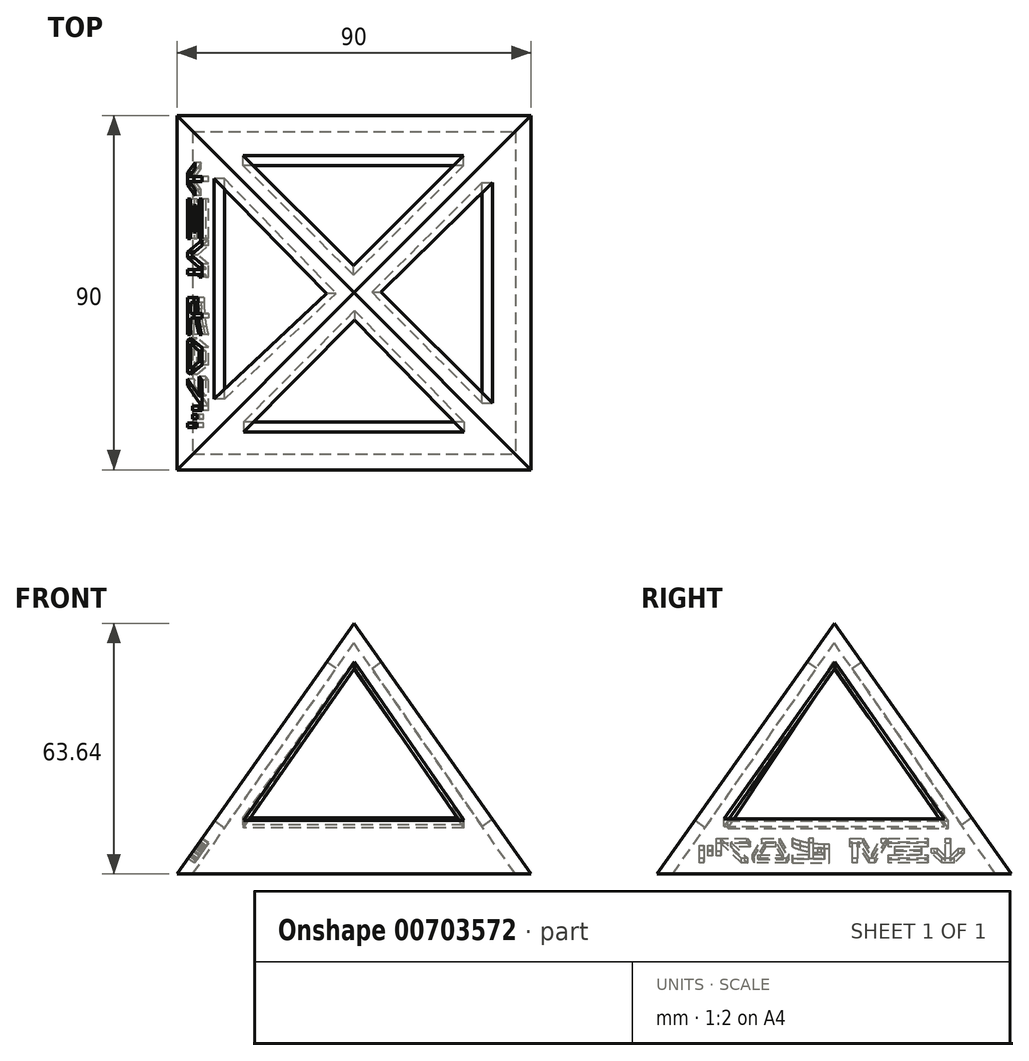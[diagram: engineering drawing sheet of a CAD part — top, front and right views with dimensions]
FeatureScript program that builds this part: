
annotation { "Feature Type Name" : "Feature", "Feature Type Description" : "" }
export const myFeature = defineFeature(function(context is Context, id is Id, definition is map)
    precondition{}
    {
        {
            var Q0;
            Q0=qCreatedBy(makeId("Top.planeOp"),FACE);
            cPlane(context, id + "F0", {"entities" : qUnion([Q0]), "cplaneType" : CPlaneType.OFFSET, "offset" : 63.64 * mm, "width" : 150 * mm, "height" : 150 * mm});
        }
        {
            var Q0;
            Q0=qCreatedBy(id+"F0.planeOp",FACE);
            var sketch = newSketch(context, id + "F1", { "sketchPlane" : qUnion([Q0])});
            skPoint(sketch, "E0", {"position": v(0, 0) * mm});
            skSolve(sketch);
        }
        {
            var Q0;
            Q0=qCreatedBy(makeId("Top.planeOp"),FACE);
            var sketch = newSketch(context, id + "F2", { "sketchPlane" : qUnion([Q0])});
            skLineSegment(sketch, "E1.bottom", {"start": v(-45, 45) * mm, "end": v(45, 45) * mm});
            skLineSegment(sketch, "E1.top", {"start": v(-45, -45) * mm, "end": v(45, -45) * mm});
            skLineSegment(sketch, "E1.left", {"start": v(-45, 45) * mm, "end": v(-45, -45) * mm});
            skLineSegment(sketch, "E1.right", {"start": v(45, 45) * mm, "end": v(45, -45) * mm});
            skPoint(sketch, "E2.orphan", {"position": v(-45, 0) * mm});
            skPoint(sketch, "E3.start.orphan", {"position": v(45, 0) * mm});
            skPoint(sketch, "E4.end.orphan", {"position": v(0, -45) * mm});
            skPoint(sketch, "E4.start.orphan", {"position": v(0, 45) * mm});
            skSolve(sketch);
        }
        {
            var Q0;
            Q0=makeQuery(id+"F2.imprint","IMPRINT",FACE,{"disambiguationData":[TD([[makeQuery(id+"F2.imprint","IMPRINT",EDGE,{"derivedFrom":sQuery(id+"F2.wireOp",EDGE,"E1.bottom")}),-1.0]])]});
            var Q1;
            Q1=sQuery(id+"F1.wireOp",VERTEX,"E0");
            loft(context, id + "F3", {"sheetProfilesArray" : [{ "sheetProfileEntities" : qUnion([Q0]) }, { "sheetProfileEntities" : qUnion([Q1]) }]});
        }
        {
            var Q0;
            Q0=qCreatedBy(makeId("Top.planeOp"),FACE);
            cPlane(context, id + "F4", {"entities" : qUnion([Q0]), "cplaneType" : CPlaneType.OFFSET, "offset" : 58.64 * mm, "width" : 150 * mm, "height" : 150 * mm});
        }
        {
            var Q0;
            Q0=qCreatedBy(id+"F4.planeOp",FACE);
            var sketch = newSketch(context, id + "F5", { "sketchPlane" : qUnion([Q0])});
            skPoint(sketch, "E5", {"position": v(0, 0) * mm});
            skSolve(sketch);
        }
        {
            var Q0;
            Q0=makeQuery(id+"F2.imprint","IMPRINT",FACE,{"disambiguationData":[TD([[makeQuery(id+"F2.imprint","IMPRINT",EDGE,{"derivedFrom":sQuery(id+"F2.wireOp",EDGE,"E1.bottom")}),-1.0]])]});
            var sketch = newSketch(context, id + "F6", { "sketchPlane" : qUnion([Q0])});
            skLineSegment(sketch, "E6.0", {"start": v(-41, 41) * mm, "end": v(-41, -41) * mm});
            skLineSegment(sketch, "E6.1", {"start": v(-41, 41) * mm, "end": v(41, 41) * mm});
            skLineSegment(sketch, "E6.2", {"start": v(41, 41) * mm, "end": v(41, -41) * mm});
            skLineSegment(sketch, "E6.3", {"start": v(-41, -41) * mm, "end": v(41, -41) * mm});
            skSolve(sketch);
        }
        {
            var Q1;
            Q1=makeQuery(id+"F6.imprint","IMPRINT",FACE,{"disambiguationData":[TD([[makeQuery(id+"F6.imprint","IMPRINT",EDGE,{"derivedFrom":sQuery(id+"F6.wireOp",EDGE,"E6.0")}),1.0]])]});
            var Q2;
            Q2=sQuery(id+"F5.wireOp",VERTEX,"E5");
            loft(context, id + "F7", {"operationType" : NewBodyOperationType.REMOVE, "sheetProfilesArray" : [{ "sheetProfileEntities" : qUnion([Q1]) }, { "sheetProfileEntities" : qUnion([Q2]) }]});
        }
        {
            var Q0;
            Q0=makeQuery(id+"F3.opLoft","SWEPT_FACE",FACE,{"disambiguationData":[OSD([sQuery(id+"F2.wireOp",EDGE,"E1.bottom"),sQuery(id+"F2.wireOp",EDGE,"E1.top"),sQuery(id+"F2.wireOp",EDGE,"E1.right")])]});
            var sketch = newSketch(context, id + "F8", { "sketchPlane" : qUnion([Q0])});
            skLineSegment(sketch, "E7.0", {"start": v(-28, -8.9) * mm, "end": v(0.15, 39.96) * mm});
            skLineSegment(sketch, "E7.1", {"start": v(27.96, -8.9) * mm, "end": v(0.15, 39.96) * mm});
            skLineSegment(sketch, "E8.0", {"start": v(27.96, -8.9) * mm, "end": v(-28, -8.9) * mm});
            skLineSegment(sketch, "E9", {"start": v(0, 51.96) * mm, "end": v(0.15, 39.96) * mm});
            skSolve(sketch);
        }
        {
            var Q0;
            Q0=makeQuery(id+"F3.opLoft","SWEPT_FACE",FACE,{"disambiguationData":[OSD([sQuery(id+"F2.wireOp",EDGE,"E1.bottom"),sQuery(id+"F2.wireOp",EDGE,"E1.left"),sQuery(id+"F2.wireOp",EDGE,"E1.right")])]});
            var sketch = newSketch(context, id + "F9", { "sketchPlane" : qUnion([Q0])});
            skLineSegment(sketch, "E10.0", {"start": v(-27.84, -8.5) * mm, "end": v(0.15, 39.96) * mm});
            skLineSegment(sketch, "E10.1", {"start": v(28.13, -8.5) * mm, "end": v(0.15, 39.96) * mm});
            skLineSegment(sketch, "E11.0", {"start": v(28.13, -8.5) * mm, "end": v(-27.84, -8.5) * mm});
            skLineSegment(sketch, "E12", {"start": v(0, 51.96) * mm, "end": v(0.15, 39.96) * mm});
            skSolve(sketch);
        }
        {
            var Q0;
            Q0=makeQuery(id+"F3.opLoft","SWEPT_FACE",FACE,{"disambiguationData":[OSD([sQuery(id+"F2.wireOp",EDGE,"E1.bottom"),sQuery(id+"F2.wireOp",EDGE,"E1.top"),sQuery(id+"F2.wireOp",EDGE,"E1.left")])]});
            var sketch = newSketch(context, id + "F10", { "sketchPlane" : qUnion([Q0])});
            skLineSegment(sketch, "E13.0", {"start": v(-28.98, -9.51) * mm, "end": v(0.15, 39.96) * mm});
            skLineSegment(sketch, "E13.1", {"start": v(26.99, -9.51) * mm, "end": v(0.15, 39.96) * mm});
            skLineSegment(sketch, "E14.0", {"start": v(26.99, -9.51) * mm, "end": v(-28.98, -9.51) * mm});
            skLineSegment(sketch, "E15", {"start": v(0, 51.96) * mm, "end": v(0.15, 39.96) * mm});
            skSolve(sketch);
        }
        {
            var Q0;
            Q0=makeQuery(id+"F3.opLoft","SWEPT_FACE",FACE,{"disambiguationData":[OSD([sQuery(id+"F2.wireOp",EDGE,"E1.top"),sQuery(id+"F2.wireOp",EDGE,"E1.left"),sQuery(id+"F2.wireOp",EDGE,"E1.right")])]});
            var sketch = newSketch(context, id + "F11", { "sketchPlane" : qUnion([Q0])});
            skLineSegment(sketch, "E16.0", {"start": v(-28.04, -9.4) * mm, "end": v(0.15, 39.96) * mm});
            skLineSegment(sketch, "E16.1", {"start": v(27.93, -9.4) * mm, "end": v(0.15, 39.96) * mm});
            skLineSegment(sketch, "E17.0", {"start": v(27.93, -9.4) * mm, "end": v(-28.04, -9.4) * mm});
            skLineSegment(sketch, "E18", {"start": v(0, 51.96) * mm, "end": v(0.15, 39.96) * mm});
            skSolve(sketch);
        }
        {
            var Q0;
            Q0=makeQuery(id+"F8.imprint","IMPRINT",FACE,{"disambiguationData":[TD([[makeQuery(id+"F8.imprint","IMPRINT",EDGE,{"derivedFrom":sQuery(id+"F8.wireOp",EDGE,"E7.0")}),-1.0]])]});
            extrude(context, id + "F12", {"entities" : qUnion([Q0]), "operationType" : NewBodyOperationType.REMOVE, "endBound" : BoundingType.SYMMETRIC, "oppositeDirection" : true, "depth" : 10 * mm, "offsetDistance" : 25 * mm});
        }
        {
            var Q0;
            Q0=makeQuery(id+"F9.imprint","IMPRINT",FACE,{"disambiguationData":[TD([[makeQuery(id+"F9.imprint","IMPRINT",EDGE,{"derivedFrom":sQuery(id+"F9.wireOp",EDGE,"E10.0")}),-1.0]])]});
            extrude(context, id + "F13", {"entities" : qUnion([Q0]), "operationType" : NewBodyOperationType.REMOVE, "oppositeDirection" : true, "depth" : 10.1 * mm, "offsetDistance" : 25 * mm});
        }
        {
            var Q0;
            Q0=makeQuery(id+"F10.imprint","IMPRINT",FACE,{"disambiguationData":[TD([[makeQuery(id+"F10.imprint","IMPRINT",EDGE,{"derivedFrom":sQuery(id+"F10.wireOp",EDGE,"E13.0")}),-1.0]])]});
            extrude(context, id + "F14", {"entities" : qUnion([Q0]), "operationType" : NewBodyOperationType.REMOVE, "oppositeDirection" : true, "depth" : 10 * mm, "offsetDistance" : 25 * mm});
        }
        {
            var Q0;
            Q0=makeQuery(id+"F11.imprint","IMPRINT",FACE,{"disambiguationData":[TD([[makeQuery(id+"F11.imprint","IMPRINT",EDGE,{"derivedFrom":sQuery(id+"F11.wireOp",EDGE,"E16.0")}),-1.0]])]});
            extrude(context, id + "F15", {"entities" : qUnion([Q0]), "operationType" : NewBodyOperationType.REMOVE, "oppositeDirection" : true, "depth" : 10 * mm, "offsetDistance" : 25 * mm});
        }
        {
            var Q0;
            Q0=makeQuery(id+"F3.opLoft","SWEPT_FACE",FACE,{"disambiguationData":[OSD([sQuery(id+"F2.wireOp",EDGE,"E1.bottom"),sQuery(id+"F2.wireOp",EDGE,"E1.top"),sQuery(id+"F2.wireOp",EDGE,"E1.left")])]});
            var sketch = newSketch(context, id + "F16", { "sketchPlane" : qUnion([Q0])});
            skLineSegment(sketch, "E19", {"start": v(-30.48, -21.2) * mm, "end": v(-27.31, -21.2) * mm});
            skLineSegment(sketch, "E20", {"start": v(-27.31, -21.2) * mm, "end": v(-24.66, -18.07) * mm});
            skLineSegment(sketch, "E21", {"start": v(-24.66, -18.07) * mm, "end": v(-26.25, -18.07) * mm});
            skLineSegment(sketch, "E22", {"start": v(-26.25, -18.07) * mm, "end": v(-28.3, -20.5) * mm});
            skLineSegment(sketch, "E23", {"start": v(-28.3, -20.5) * mm, "end": v(-28.3, -14.95) * mm});
            skLineSegment(sketch, "E24", {"start": v(-28.3, -14.95) * mm, "end": v(-29.48, -14.95) * mm});
            skLineSegment(sketch, "E25", {"start": v(-29.48, -14.95) * mm, "end": v(-29.48, -20.5) * mm});
            skLineSegment(sketch, "E26", {"start": v(-29.48, -20.5) * mm, "end": v(-31.54, -18.07) * mm});
            skLineSegment(sketch, "E27", {"start": v(-31.54, -18.07) * mm, "end": v(-33.13, -18.07) * mm});
            skLineSegment(sketch, "E28", {"start": v(-33.13, -18.07) * mm, "end": v(-30.48, -21.2) * mm});
            skLineSegment(sketch, "E29", {"start": v(-13.74, -16.13) * mm, "end": v(-13.74, -14.95) * mm});
            skLineSegment(sketch, "E30", {"start": v(-13.74, -14.95) * mm, "end": v(-23.85, -14.95) * mm});
            skLineSegment(sketch, "E31", {"start": v(-23.85, -14.95) * mm, "end": v(-23.85, -16.13) * mm});
            skLineSegment(sketch, "E32", {"start": v(-23.85, -16.13) * mm, "end": v(-13.74, -16.13) * mm});
            skLineSegment(sketch, "E33", {"start": v(-13.74, -21.2) * mm, "end": v(-13.74, -20.01) * mm});
            skLineSegment(sketch, "E34", {"start": v(-13.74, -20.01) * mm, "end": v(-23.85, -20.01) * mm});
            skLineSegment(sketch, "E35", {"start": v(-23.85, -20.01) * mm, "end": v(-23.85, -21.2) * mm});
            skLineSegment(sketch, "E36", {"start": v(-23.85, -21.2) * mm, "end": v(-13.74, -21.2) * mm});
            skLineSegment(sketch, "E37", {"start": v(-15.46, -18.66) * mm, "end": v(-15.46, -17.48) * mm});
            skLineSegment(sketch, "E38", {"start": v(-15.46, -17.48) * mm, "end": v(-22.13, -17.48) * mm});
            skLineSegment(sketch, "E39", {"start": v(-22.13, -17.48) * mm, "end": v(-22.13, -18.66) * mm});
            skLineSegment(sketch, "E40", {"start": v(-22.13, -18.66) * mm, "end": v(-15.46, -18.66) * mm});
            skLineSegment(sketch, "E41", {"start": v(-9.62, -19.72) * mm, "end": v(-11.96, -14.95) * mm});
            skLineSegment(sketch, "E42", {"start": v(-11.96, -14.95) * mm, "end": v(-13.4, -14.95) * mm});
            skLineSegment(sketch, "E43", {"start": v(-13.4, -14.95) * mm, "end": v(-10.33, -21.2) * mm});
            skLineSegment(sketch, "E44", {"start": v(-10.33, -21.2) * mm, "end": v(-8.9, -21.2) * mm});
            skLineSegment(sketch, "E45", {"start": v(-8.9, -21.2) * mm, "end": v(-6.42, -16.13) * mm});
            skLineSegment(sketch, "E46", {"start": v(-6.42, -16.13) * mm, "end": v(-5.84, -16.13) * mm});
            skLineSegment(sketch, "E47", {"start": v(-5.84, -16.13) * mm, "end": v(-5.84, -21.2) * mm});
            skLineSegment(sketch, "E48", {"start": v(-5.84, -21.2) * mm, "end": v(-4.66, -21.2) * mm});
            skLineSegment(sketch, "E49", {"start": v(-4.66, -21.2) * mm, "end": v(-4.66, -16.13) * mm});
            skLineSegment(sketch, "E50", {"start": v(-4.66, -16.13) * mm, "end": v(-3.94, -16.13) * mm});
            skLineSegment(sketch, "E51", {"start": v(-3.94, -16.13) * mm, "end": v(-3.94, -14.95) * mm});
            skLineSegment(sketch, "E52", {"start": v(-3.94, -14.95) * mm, "end": v(-7.28, -14.95) * mm});
            skLineSegment(sketch, "E53", {"start": v(-7.28, -14.95) * mm, "end": v(-9.62, -19.72) * mm});
            skLineSegment(sketch, "E54", {"start": v(2.43, -20.01) * mm, "end": v(5.3, -20.01) * mm});
            skLineSegment(sketch, "E55", {"start": v(5.3, -20.01) * mm, "end": v(5.3, -17.82) * mm});
            skLineSegment(sketch, "E56", {"start": v(2.43, -17.95) * mm, "end": v(2.43, -20.01) * mm});
            skLineSegment(sketch, "E57", {"start": v(5.3, -16.6) * mm, "end": v(5.3, -14.95) * mm});
            skLineSegment(sketch, "E58", {"start": v(5.3, -14.95) * mm, "end": v(6.48, -14.95) * mm});
            skLineSegment(sketch, "E59", {"start": v(6.48, -14.95) * mm, "end": v(6.48, -16.4) * mm});
            skLineSegment(sketch, "E60", {"start": v(10.66, -14.95) * mm, "end": v(10.66, -16.14) * mm});
            skLineSegment(sketch, "E61", {"start": v(6.48, -17.65) * mm, "end": v(6.48, -20.01) * mm});
            skLineSegment(sketch, "E62", {"start": v(6.48, -20.01) * mm, "end": v(10.66, -20.01) * mm});
            skLineSegment(sketch, "E63", {"start": v(10.66, -20.01) * mm, "end": v(10.66, -21.2) * mm});
            skLineSegment(sketch, "E64", {"start": v(10.66, -21.2) * mm, "end": v(1.25, -21.2) * mm});
            skLineSegment(sketch, "E65", {"start": v(1.25, -21.2) * mm, "end": v(1.25, -16.76) * mm});
            skLineSegment(sketch, "E66", {"start": v(1.25, -16.76) * mm, "end": v(2.43, -16.76) * mm});
            skLineSegment(sketch, "E67", {"start": v(12.92, -20.01) * mm, "end": v(14.82, -16.13) * mm});
            skLineSegment(sketch, "E68", {"start": v(14.82, -16.13) * mm, "end": v(17.48, -16.13) * mm});
            skLineSegment(sketch, "E69", {"start": v(17.48, -16.13) * mm, "end": v(19.37, -20.01) * mm});
            skLineSegment(sketch, "E70", {"start": v(19.37, -20.01) * mm, "end": v(12.92, -20.01) * mm});
            skLineSegment(sketch, "E71", {"start": v(20.26, -21.2) * mm, "end": v(20.83, -20.04) * mm});
            skLineSegment(sketch, "E72", {"start": v(20.83, -20.04) * mm, "end": v(18.33, -14.95) * mm});
            skLineSegment(sketch, "E73", {"start": v(18.33, -14.95) * mm, "end": v(13.96, -14.95) * mm});
            skLineSegment(sketch, "E74", {"start": v(13.96, -14.95) * mm, "end": v(11.5, -19.98) * mm});
            skLineSegment(sketch, "E75", {"start": v(11.5, -19.98) * mm, "end": v(12.09, -21.2) * mm});
            skLineSegment(sketch, "E76", {"start": v(12.09, -21.2) * mm, "end": v(20.26, -21.2) * mm});
            skLineSegment(sketch, "E77", {"start": v(23.56, -21.2) * mm, "end": v(28.74, -15.1) * mm});
            skLineSegment(sketch, "E78", {"start": v(28.86, -14.95) * mm, "end": v(22.22, -14.95) * mm});
            skLineSegment(sketch, "E79", {"start": v(22.22, -14.95) * mm, "end": v(21.22, -16.13) * mm});
            skLineSegment(sketch, "E80", {"start": v(21.22, -16.13) * mm, "end": v(26.26, -16.13) * mm});
            skLineSegment(sketch, "E81", {"start": v(26.26, -16.13) * mm, "end": v(21.97, -21.2) * mm});
            skLineSegment(sketch, "E82", {"start": v(21.97, -21.2) * mm, "end": v(23.56, -21.2) * mm});
            skLineSegment(sketch, "E83", {"start": v(29.92, -19) * mm, "end": v(29.92, -14.95) * mm});
            skLineSegment(sketch, "E84", {"start": v(29.92, -14.95) * mm, "end": v(28.74, -14.95) * mm});
            skLineSegment(sketch, "E85", {"start": v(28.74, -15.1) * mm, "end": v(28.74, -19) * mm});
            skLineSegment(sketch, "E86", {"start": v(28.74, -19) * mm, "end": v(29.92, -19) * mm});
            skLineSegment(sketch, "E87", {"start": v(34.22, -21.2) * mm, "end": v(34.22, -17.13) * mm});
            skLineSegment(sketch, "E88", {"start": v(34.22, -17.13) * mm, "end": v(33.04, -17.13) * mm});
            skLineSegment(sketch, "E89", {"start": v(33.04, -17.13) * mm, "end": v(33.04, -21.2) * mm});
            skLineSegment(sketch, "E90", {"start": v(33.04, -21.2) * mm, "end": v(34.22, -21.2) * mm});
            skLineSegment(sketch, "E91", {"start": v(32.07, -19) * mm, "end": v(32.07, -17.13) * mm});
            skLineSegment(sketch, "E92", {"start": v(32.07, -17.13) * mm, "end": v(30.89, -17.13) * mm});
            skLineSegment(sketch, "E93", {"start": v(30.89, -17.13) * mm, "end": v(30.89, -19) * mm});
            skLineSegment(sketch, "E94", {"start": v(30.89, -19) * mm, "end": v(32.07, -19) * mm});
            skFitSpline(sketch, "E95", {"points": [v(5.3, -17.82) * mm, v(5.1, -17.85) * mm, v(4.72, -17.9) * mm, v(4.34, -17.92) * mm, v(4.16, -17.93) * mm]});
            skFitSpline(sketch, "E96", {"points": [v(4.16, -17.93) * mm, v(4, -17.94) * mm, v(3.7, -17.95) * mm, v(3.4, -17.96) * mm, v(3.25, -17.96) * mm]});
            skFitSpline(sketch, "E97", {"points": [v(3.25, -17.96) * mm, v(3.1, -17.97) * mm, v(2.83, -17.97) * mm, v(2.56, -17.96) * mm, v(2.43, -17.95) * mm]});
            skFitSpline(sketch, "E98", {"points": [v(2.43, -16.76) * mm, v(2.56, -16.77) * mm, v(2.82, -16.78) * mm, v(3.1, -16.78) * mm, v(3.23, -16.77) * mm]});
            skFitSpline(sketch, "E99", {"points": [v(3.23, -16.77) * mm, v(3.37, -16.77) * mm, v(3.67, -16.76) * mm, v(3.98, -16.74) * mm, v(4.14, -16.73) * mm]});
            skFitSpline(sketch, "E100", {"points": [v(4.14, -16.73) * mm, v(4.33, -16.71) * mm, v(4.71, -16.68) * mm, v(5.1, -16.63) * mm, v(5.3, -16.6) * mm]});
            skFitSpline(sketch, "E101", {"points": [v(6.48, -16.4) * mm, v(6.81, -16.33) * mm, v(7.5, -16.18) * mm, v(8.18, -15.97) * mm, v(8.52, -15.86) * mm]});
            skFitSpline(sketch, "E102", {"points": [v(8.52, -15.86) * mm, v(8.88, -15.74) * mm, v(9.62, -15.48) * mm, v(10.3, -15.13) * mm, v(10.66, -14.95) * mm]});
            skFitSpline(sketch, "E103", {"points": [v(10.66, -16.14) * mm, v(10.33, -16.3) * mm, v(9.66, -16.64) * mm, v(8.96, -16.92) * mm, v(8.6, -17.05) * mm]});
            skFitSpline(sketch, "E104", {"points": [v(8.6, -17.05) * mm, v(8.25, -17.18) * mm, v(7.56, -17.42) * mm, v(6.84, -17.57) * mm, v(6.48, -17.65) * mm]});
            skSolve(sketch);
        }
        {
            var Q0;
            {var subQ3=sQuery(id+"F16.wireOp",EDGE,"E83");Q0=makeQuery(id+"F16.imprint","IMPRINT",FACE,{"disambiguationData":[TD([[makeQuery(id+"F16.imprint","IMPRINT",EDGE,{"derivedFrom":subQ3}),1.0]])]});}
            var Q1;
            Q1=makeQuery(id+"F16.imprint","IMPRINT",FACE,{"disambiguationData":[TD([[makeQuery(id+"F16.imprint","IMPRINT",EDGE,{"derivedFrom":sQuery(id+"F16.wireOp",EDGE,"E91")}),1.0]])]});
            var Q2;
            Q2=makeQuery(id+"F16.imprint","IMPRINT",FACE,{"disambiguationData":[TD([[makeQuery(id+"F16.imprint","IMPRINT",EDGE,{"derivedFrom":sQuery(id+"F16.wireOp",EDGE,"E87")}),1.0]])]});
            var Q3;
            Q3=makeQuery(id+"F16.imprint","IMPRINT",FACE,{"disambiguationData":[TD([[makeQuery(id+"F16.imprint","IMPRINT",EDGE,{"derivedFrom":sQuery(id+"F16.wireOp",EDGE,"E67")}),1.0]])]});
            var Q4;
            Q4=makeQuery(id+"F16.imprint","IMPRINT",FACE,{"disambiguationData":[TD([[makeQuery(id+"F16.imprint","IMPRINT",EDGE,{"derivedFrom":sQuery(id+"F16.wireOp",EDGE,"E54")}),-1.0]])]});
            var Q5;
            Q5=makeQuery(id+"F16.imprint","IMPRINT",FACE,{"disambiguationData":[TD([[makeQuery(id+"F16.imprint","IMPRINT",EDGE,{"derivedFrom":sQuery(id+"F16.wireOp",EDGE,"E41")}),1.0]])]});
            var Q6;
            Q6=makeQuery(id+"F16.imprint","IMPRINT",FACE,{"disambiguationData":[TD([[makeQuery(id+"F16.imprint","IMPRINT",EDGE,{"derivedFrom":sQuery(id+"F16.wireOp",EDGE,"E29")}),1.0]])]});
            var Q7;
            Q7=makeQuery(id+"F16.imprint","IMPRINT",FACE,{"disambiguationData":[TD([[makeQuery(id+"F16.imprint","IMPRINT",EDGE,{"derivedFrom":sQuery(id+"F16.wireOp",EDGE,"E37")}),1.0]])]});
            var Q8;
            Q8=makeQuery(id+"F16.imprint","IMPRINT",FACE,{"disambiguationData":[TD([[makeQuery(id+"F16.imprint","IMPRINT",EDGE,{"derivedFrom":sQuery(id+"F16.wireOp",EDGE,"E33")}),1.0]])]});
            var Q9;
            Q9=makeQuery(id+"F16.imprint","IMPRINT",FACE,{"disambiguationData":[TD([[makeQuery(id+"F16.imprint","IMPRINT",EDGE,{"derivedFrom":sQuery(id+"F16.wireOp",EDGE,"E19")}),1.0]])]});
            extrude(context, id + "F17", {"entities" : qUnion([Q0, Q1, Q2, Q3, Q4, Q5, Q6, Q7, Q8, Q9]), "operationType" : NewBodyOperationType.REMOVE, "oppositeDirection" : true, "depth" : 2 * mm, "offsetDistance" : 25 * mm});
        }
    });
